# Revit family: xxxBi_Level_Drinking_Fountain-Refrigerated-Murdock_Mfg-A172408S-FG-VR
name_source: partatom
category: Plumbing Fixtures
units: mm (PartAtom-declared; Revit-internal decimal feet)

## family parameters
Cut with Voids When Loaded = Yes
Host = Face
OmniClass Number = 23.65.70.14.11
OmniClass Title = Drinking Fountains/Coolers
Part Type = Normal
Room Calculation Point = No
Round Connector Dimension = Use Diameter
Shared = Yes

## types (1)
- A172408S-FG-VR
    -220V 220 Volt / 50 Hz Compressor = No
    -CSC3 Concealed Support Carrier = No
    -RBL Reverse Bi-level = No
    -SK9 Skirt Kit, Stainless Steel, For Upper Unit = No
    -WB2 Wall Bezel, Stainless Steel = No
    -WF1 1500 Gallon Capacity, NSF 42+53, 1 Micron Lead Reduction Filter = No
    ADA Compliant = Yes
    Activation = Push Button
    Assembly Code = D2010800
    CW Connection = Yes
    CWFU = 1
    Cold Water Connection Diameter = 3/8"
    Default Elevation = 0"
    Description = 14GA Stainless Steel, Vandal-Resistant, Wall-Mounted, Bi-Level Drinking Fountain - In-Unit Refrigeration (8GPH), ADA
    Electric Connection Height = 16 7/8"
    Finish = Stainless Steel-Murdock-Type 304-Satin
    Finish- Push Button = Brass-Murdock-Chrome Plated
    Finish-Bubbler = Stainless Steel-Murdock-Polished
    Full Load Amps = 4.4
    GPH = 8.0
    HW Connection = No
    HWFU = 0
    Height From Floor Level = 33"
    IAPMO Compliance = NSF/ANSI 61, Federal Public Law 111-380 (No Lead)
    Installation Instruction Link = https://www.murdockmfg.com
    Installation Type = Wall Mounted
    Left Bubbler = 4 1/16"
    Left Drain = 13 9/16"
    Left Ftn = 41 3/4"
    Length = 18 3/4"
    Manufacturer = Murdock Manufacturing
    Material = Stainless Steel-Murdock-Type 304-Satin
    Model = A172408S-FG-VR
    Outlet Connections Offset = 4 1/4"
    Price = Prices may vary. Please consult Manufacturer Representative for most up-to-date price list.
    Product Documentation Link = https://www.murdockmfg.com
    Product Page URL = https://www.murdockmfg.com
    Revised Date = 10/04/2022
    Right Bubbler = 14 9/16"
    Right Drain = 5 1/16"
    Right Ftn = 33 1/2"
    Shipping Weight = 140 lbs.
    URL = https://www.murdockmfg.com
    Vent Connection = No
    Voltage Nominal = 220 V
    WFU = 1.5
    Waste Connection = Yes
    Waste Connection Diameter = 1 1/4"
    Waste Connection Height = 22 1/4"
    Water Inlet Height = 22 1/4"
    Water Pressure = 20-105 psig
    Watts = 400 W
    Width = 37 1/8"
    cUPC Compliant = Yes

## geometry (parser evidence)
native form markers: Sweep x2
no freeform markers — native parametric forms only
